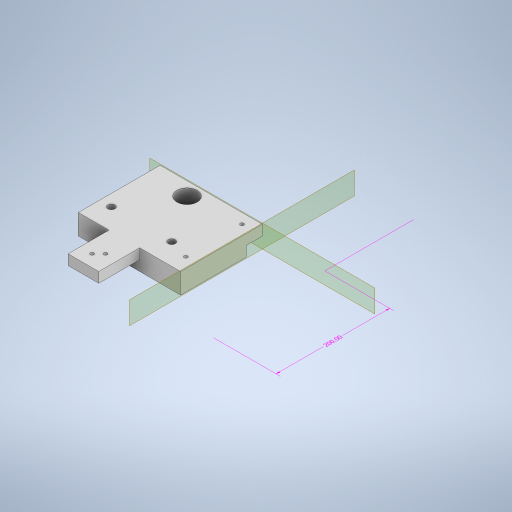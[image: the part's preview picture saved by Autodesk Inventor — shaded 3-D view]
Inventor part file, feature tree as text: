
AUTODESK INVENTOR PART (.ipt)
format: ipt  version: 2023 (Build 270158000, 158)  size: 433,152 bytes
history: native  units: mm
features: sketch x10, extrude x5, hole x5, other x3, plane x2, split x2
ambient origin geometry x8: Origin, YZ Plane, XZ Plane, XY Plane, X Axis, Y Axis, Z Axis, Center Point
bodies: Body1 (feature_tree)
feature tree (27):
  other  "Sólido1"
  other  "Anotaciones"
  extrude  "Extrusión1"  Depth=160.0mm
  extrude  "Extrusión2"  Depth=30.0mm
  hole  "Agujero1"  [1 undecoded]
  extrude  "Extrusión3"  Depth=11.75mm
  hole  "Agujero2"  [1 undecoded]
  hole  "Agujero3"  [1 undecoded]
  extrude  "Extrusión4"  TaperAngle=0.0deg  [1 undecoded]
  plane  "Plano de trabajo1"
  plane  "Plano de trabajo2"
  hole  "Agujero4"  [1 undecoded]
  hole  "Agujero5"  [1 undecoded]
  extrude  "Extrusión5"  Depth=70.0mm
  split  "Dividir1"
  split  "Dividir2"
  sketch  "Boceto1"  dims[d0=200.0mm d1=160.0mm]
  sketch  "Boceto2"  dims[d2=20.0mm d3=0.0mm d4=30.0mm]
  sketch  "Boceto3"  dims[d5=40.0mm d6=10.0mm d7=0.0mm]
  sketch  "Boceto4"  dims[d23=21.75mm d24=11.75mm]
  sketch  "Boceto5"  dims[d26=11.75mm]
  sketch  "Boceto6"  dims[d27=3.5mm d28=6.0mm d29=4.0mm d30=2.0mm d31=90.0deg d32=8.0mm d33=20.594885mm d34=30.0mm]
  sketch  "Boceto7"  dims[d35=10.0mm d36=30.0mm]
  sketch  "Boceto8"  dims[d37=40.0mm d38=0.0mm]
  sketch  "Boceto9"  dims[d39=10.0mm d40=10.0mm d41=40.0mm d42=0.0mm d43=6.5mm d44=6.5mm d45=3.5mm d46=3.5mm d47=11.749873mm d48=11.75mm d49=0.0mm]
  sketch  "Boceto10"  dims[d50=11.75mm d51=0.0mm d52=3.5mm d53=6.0mm d54=4.0mm d55=2.0mm d56=90.0deg d57=8.0mm d58=20.594885mm d59=7.0mm d60=7.0mm d61=7.0mm d62=39.0mm d63=46.0mm d64=59.0mm d65=46.0mm d66=39.0mm d67=59.0mm d68=52.0mm d69=70.0mm d70=22.0mm d71=42.0mm d72=3.5mm d73=3.5mm d74=3.5mm d75=3.5mm d76=3.5mm d77=6.0mm d78=4.0mm d79=2.0mm d80=90.0deg d81=8.0mm d82=20.594885mm d83=7.0mm d84=7.0mm d85=7.0mm d86=39.0mm d87=46.0mm d88=59.0mm d89=46.0mm d90=39.0mm d91=59.0mm d92=20.0mm d93=0.0mm d97=40.000127mm d98=10.0mm d99=30.0mm d100=10.0mm d101=5.0mm d102=5.0mm d103=5.0mm d104=5.0mm d105=45.0deg d106=45.0deg d107=10.0mm d108=10.0mm d109=30.0mm d110=5.0mm d111=5.0mm d112=5.0mm d113=5.0mm d114=10.0mm d115=30.0mm d116=5.0mm d117=5.0mm d118=5.0mm d119=5.0mm d120=10.0mm d121=3.5mm d122=6.0mm d123=4.0mm d124=2.0mm d125=90.0deg d126=8.0mm d127=20.594885mm d128=3.5mm d129=10.0mm d130=10.0mm d131=3.5mm d132=6.0mm d133=4.0mm d134=2.0mm d135=90.0deg d136=8.0mm d137=20.594885mm d138=32.0mm d139=32.0mm d140=10.0mm d141=0.0mm d142=17.37633mm d143=12.709242mm d144=6.683722mm d145=12.708891mm d146=5.220756mm d147=1.603663mm d148=2.153068mm d149=6.490327mm d94=6.100674mm d95=2.550465mm d96=200.0mm]
  other  "Cota lineal 1"
note: 6 required parameter values undecoded (feature->parameter linkage not recoverable at this tier; creation-order binding heuristic only, values carry confidence <= 0.55)
